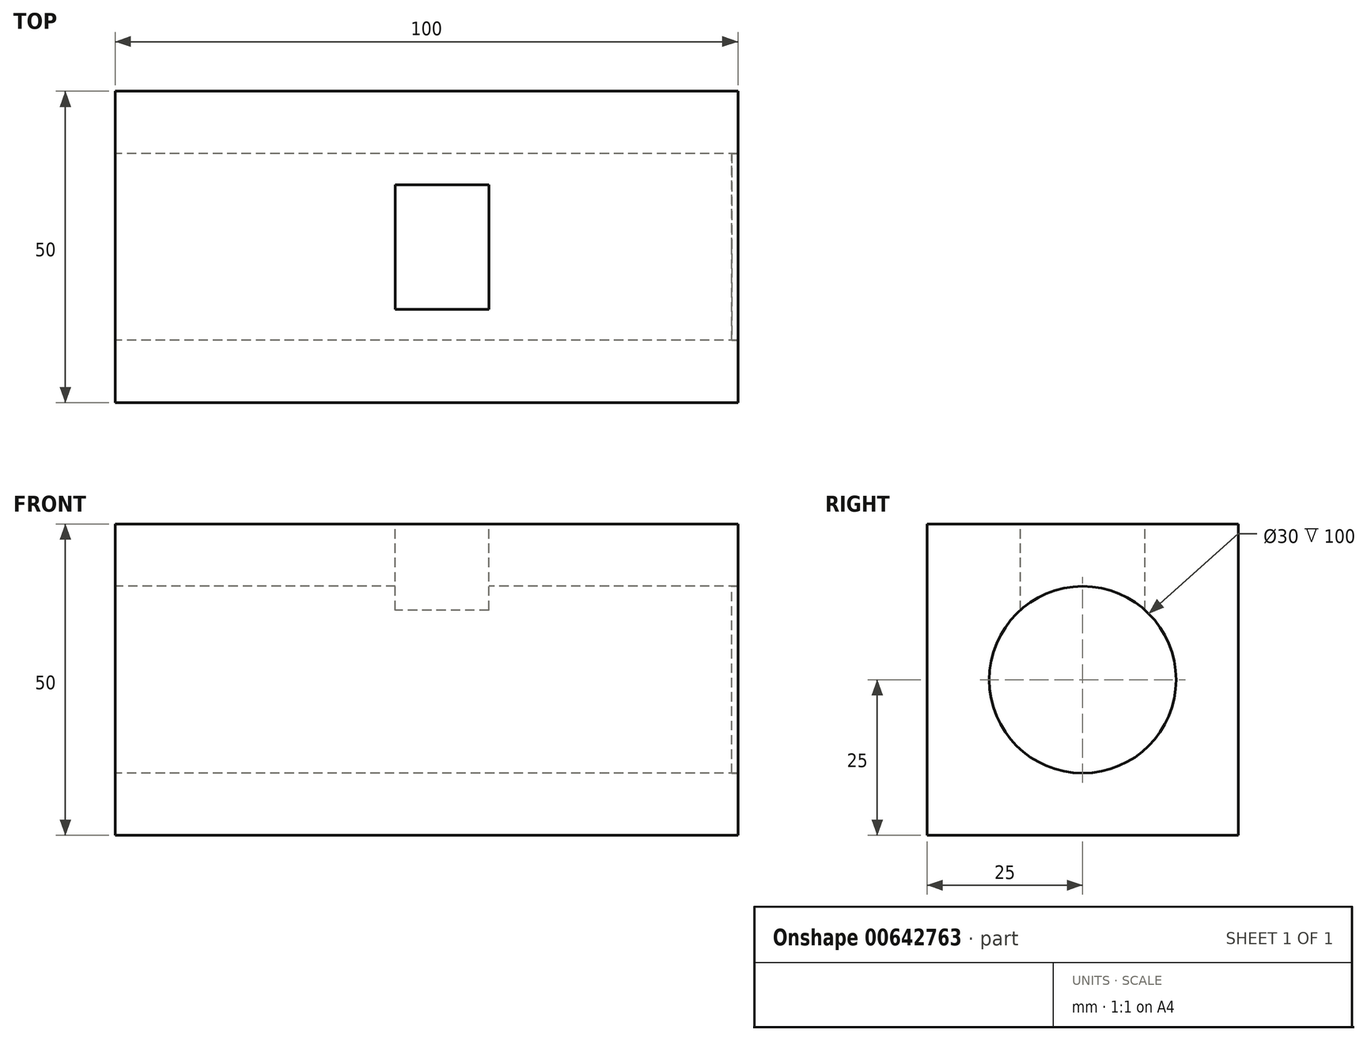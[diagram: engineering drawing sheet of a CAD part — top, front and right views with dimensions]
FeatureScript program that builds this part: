
annotation { "Feature Type Name" : "Feature", "Feature Type Description" : "" }
export const myFeature = defineFeature(function(context is Context, id is Id, definition is map)
    precondition{}
    {
        {
            var Q0;
            Q0=qCreatedBy(makeId("Right.planeOp"),FACE);
            var sketch = newSketch(context, id + "F0", { "sketchPlane" : qUnion([Q0])});
            skLineSegment(sketch, "E0.bottom", {"start": v(-25, 25) * mm, "end": v(25, 25) * mm});
            skLineSegment(sketch, "E0.top", {"start": v(-25, -25) * mm, "end": v(25, -25) * mm});
            skLineSegment(sketch, "E0.left", {"start": v(-25, 25) * mm, "end": v(-25, -25) * mm});
            skLineSegment(sketch, "E0.right", {"start": v(25, 25) * mm, "end": v(25, -25) * mm});
            skCircle(sketch, "E1", {"center": v(0, 0) * mm, "radius": 15 * mm});
            skSolve(sketch);
        }
        {
            var Q0;
            Q0 = qSketchRegion(id + "F0", true);
            extrude(context, id + "F1", {"entities" : qUnion([Q0]), "depth" : 100 * mm, "offsetDistance" : 25 * mm});
        }
        {
            var Q0;
            Q0=makeQuery(id+"F1.opExtrude","SWEPT_FACE",FACE,{"disambiguationData":[OSD([sQuery(id+"F0.wireOp",EDGE,"E0.bottom")])]});
            var sketch = newSketch(context, id + "F2", { "sketchPlane" : qUnion([Q0])});
            skLineSegment(sketch, "E2.bottom", {"start": v(45, 10) * mm, "end": v(60, 10) * mm});
            skLineSegment(sketch, "E2.top", {"start": v(45, -10) * mm, "end": v(60, -10) * mm});
            skLineSegment(sketch, "E2.left", {"start": v(45, 10) * mm, "end": v(45, -10) * mm});
            skLineSegment(sketch, "E2.right", {"start": v(60, 10) * mm, "end": v(60, -10) * mm});
            skSolve(sketch);
        }
        {
            var Q0;
            Q0 = qSketchRegion(id + "F2", true);
            extrude(context, id + "F3", {"entities" : qUnion([Q0]), "operationType" : NewBodyOperationType.REMOVE, "oppositeDirection" : true, "depth" : 25 * mm, "offsetDistance" : 25 * mm});
        }
        {
            var Q0;
            Q0=makeQuery(id+"F1.opExtrude","CAP_FACE",FACE,{"disambiguationData":[OSD([sQuery(id+"F0.wireOp",EDGE,"E0.bottom"),sQuery(id+"F0.wireOp",EDGE,"E0.top"),sQuery(id+"F0.wireOp",EDGE,"E0.left"),sQuery(id+"F0.wireOp",EDGE,"E0.right"),sQuery(id+"F0.wireOp",EDGE,"E1")])],"isStart":false});
            var sketch = newSketch(context, id + "F4", { "sketchPlane" : qUnion([Q0])});
            skCircle(sketch, "E3", {"center": v(0, 0) * mm, "radius": 15 * mm});
            skSolve(sketch);
        }
        {
            var Q0;
            Q0 = qSketchRegion(id + "F4", true);
            extrude(context, id + "F5", {"entities" : qUnion([Q0]), "oppositeDirection" : true, "depth" : 1 * mm, "offsetDistance" : 25 * mm});
        }
    });
